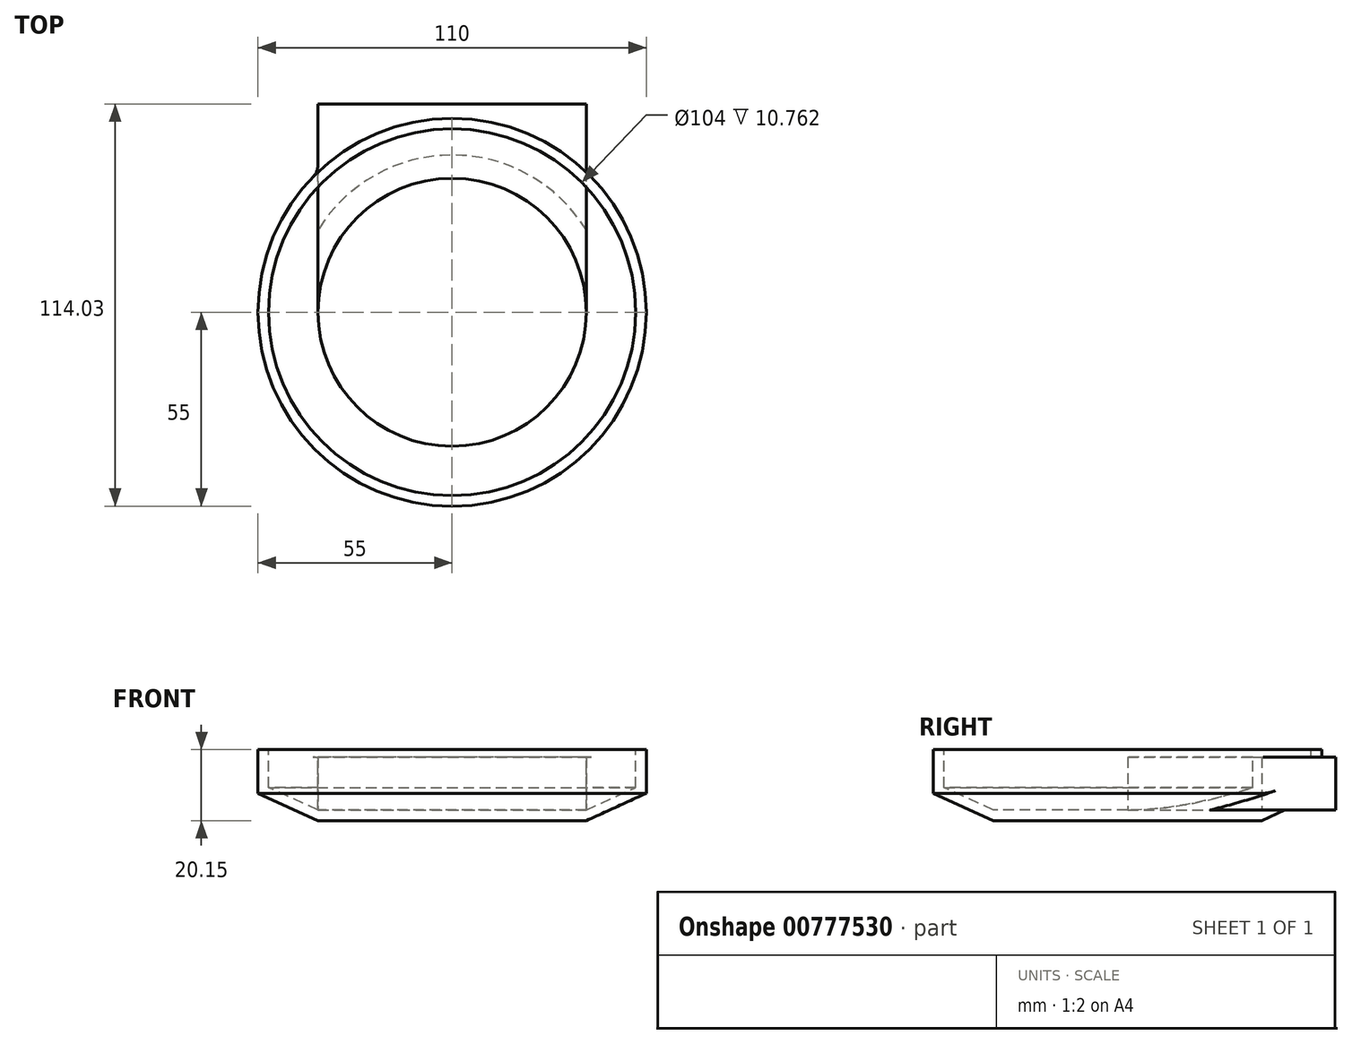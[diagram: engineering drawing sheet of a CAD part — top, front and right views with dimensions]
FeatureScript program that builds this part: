
annotation { "Feature Type Name" : "Feature", "Feature Type Description" : "" }
export const myFeature = defineFeature(function(context is Context, id is Id, definition is map)
    precondition{}
    {
        {
            var Q0;
            Q0=qCreatedBy(makeId("Front.planeOp"),FACE);
            var sketch = newSketch(context, id + "F0", { "sketchPlane" : qUnion([Q0])});
            skLineSegment(sketch, "E0", {"start": v(0, 0) * mm, "end": v(38, 0) * mm});
            skLineSegment(sketch, "E1", {"start": v(38, 0) * mm, "end": v(55, 7.76) * mm});
            skLineSegment(sketch, "E2", {"start": v(55, 7.76) * mm, "end": v(55, 20.15) * mm});
            skLineSegment(sketch, "E3", {"start": v(55, 20.15) * mm, "end": v(52, 20.15) * mm});
            skLineSegment(sketch, "E4", {"start": v(52, 20.15) * mm, "end": v(52, 9.4) * mm});
            skLineSegment(sketch, "E5", {"start": v(52, 9.4) * mm, "end": v(38, 3) * mm});
            skLineSegment(sketch, "E6", {"start": v(38, 3) * mm, "end": v(0, 3) * mm});
            skLineSegment(sketch, "E7", {"start": v(0, 3) * mm, "end": v(0, 0) * mm});
            skSolve(sketch);
        }
        {
            var Q0;
            Q0=makeQuery(id+"F0.imprint","IMPRINT",FACE,{"disambiguationData":[TD([[makeQuery(id+"F0.imprint","IMPRINT",EDGE,{"derivedFrom":sQuery(id+"F0.wireOp",EDGE,"E0")}),1.0]])]});
            var Q1;
            Q1=sQuery(id+"F0.wireOp",EDGE,"E7");
            revolve(context, id + "F1", {"surfaceOperationType" : NewSurfaceOperationType.NEW, "entities" : qUnion([Q0]), "axis" : qUnion([Q1]), "revolveType" : RevolveType.FULL});
        }
        {
            var Q0;
            Q0=makeQuery(id+"F1.opRevolve","SWEPT_FACE",FACE,{"disambiguationData":[OSD([sQuery(id+"F0.wireOp",EDGE,"E6")])]});
            var sketch = newSketch(context, id + "F2", { "sketchPlane" : qUnion([Q0])});
            skLineSegment(sketch, "E8", {"start": v(-38, 0) * mm, "end": v(-38, 59.03) * mm});
            skLineSegment(sketch, "E9", {"start": v(-38, 59.03) * mm, "end": v(38, 59.03) * mm});
            skLineSegment(sketch, "E10", {"start": v(38, 59.03) * mm, "end": v(38, 0) * mm});
            skLineSegment(sketch, "E11", {"start": v(38, 0) * mm, "end": v(-38, 0) * mm});
            skSolve(sketch);
        }
        {
            var Q0;
            {var subQ0=sQuery(id+"F2.wireOp",EDGE,"E8");Q0=makeQuery(id+"F2.imprint","IMPRINT",FACE,{"disambiguationData":[TD([[makeQuery(id+"F2.imprint","IMPRINT",EDGE,{"derivedFrom":subQ0}),-1.0]])]});}
            extrude(context, id + "F3", {"entities" : qUnion([Q0]), "operationType" : NewBodyOperationType.ADD, "depth" : 15 * mm, "offsetDistance" : 25 * mm});
        }
        {
            var Q0;
            Q0=makeQuery(id+"F3.boolean.opBoolean","INTERSECT",EDGE,{"derivedFrom":[makeQuery(id+"F1.opRevolve","SWEPT_FACE",FACE,{"disambiguationData":[OSD([sQuery(id+"F0.wireOp",EDGE,"E2")])]}),makeQuery(id+"F3.opExtrude","SWEPT_FACE",FACE,{"disambiguationData":[OSD([sQuery(id+"F2.wireOp",EDGE,"E10")])]})]});
            var Q1;
            Q1=makeQuery(id+"F3.boolean.opBoolean","INTERSECT",EDGE,{"derivedFrom":[makeQuery(id+"F1.opRevolve","SWEPT_FACE",FACE,{"disambiguationData":[OSD([sQuery(id+"F0.wireOp",EDGE,"E2")])]}),makeQuery(id+"F3.opExtrude","SWEPT_FACE",FACE,{"disambiguationData":[OSD([sQuery(id+"F2.wireOp",EDGE,"E8")])]})]});
            fillet(context, id + "F4", {"entities" : qUnion([Q0, Q1]), "radius" : 5 * mm, "tangentPropagation" : true, "allowEdgeOverflow" : false});
        }
    });
